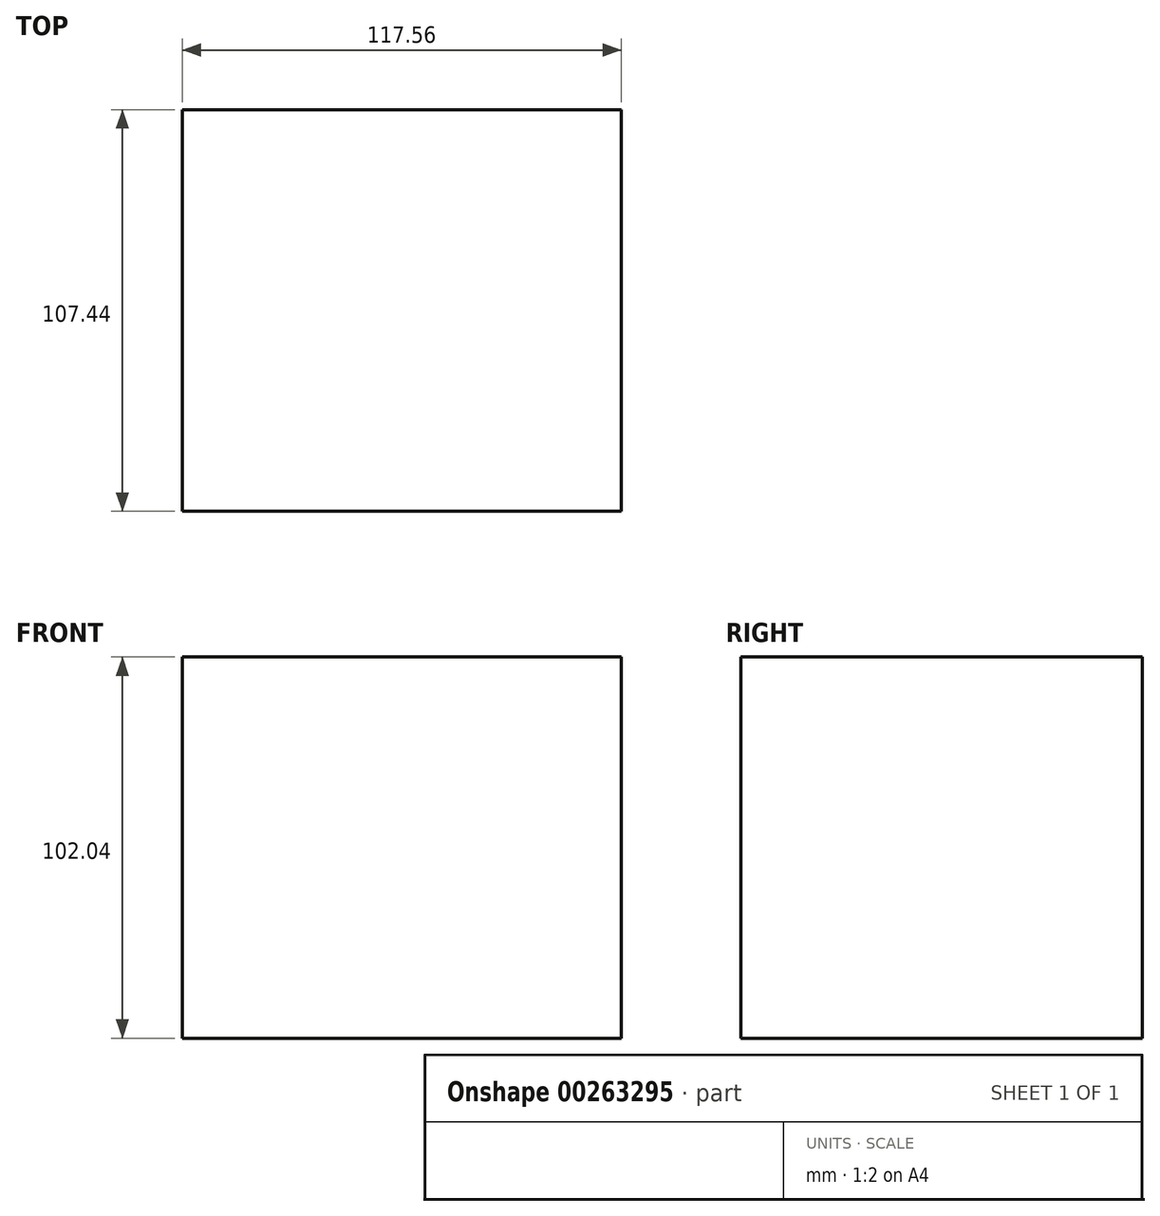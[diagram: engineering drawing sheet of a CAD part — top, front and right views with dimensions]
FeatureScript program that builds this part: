
annotation { "Feature Type Name" : "Feature", "Feature Type Description" : "" }
export const myFeature = defineFeature(function(context is Context, id is Id, definition is map)
    precondition{}
    {
        {
            var Q0;
            Q0=qCreatedBy(makeId("Front.planeOp"),FACE);
            var sketch = newSketch(context, id + "F0", { "sketchPlane" : qUnion([Q0])});
            skLineSegment(sketch, "E0.bottom", {"start": v(-60.76, 49.92) * mm, "end": v(56.8, 49.92) * mm});
            skLineSegment(sketch, "E0.top", {"start": v(-60.76, -52.12) * mm, "end": v(56.8, -52.12) * mm});
            skLineSegment(sketch, "E0.left", {"start": v(-60.76, 49.92) * mm, "end": v(-60.76, -52.12) * mm});
            skLineSegment(sketch, "E0.right", {"start": v(56.8, 49.92) * mm, "end": v(56.8, -52.12) * mm});
            skSolve(sketch);
        }
        {
            var Q0;
            Q0=makeQuery(id+"F0.imprint","IMPRINT",FACE,{"disambiguationData":[TD([[makeQuery(id+"F0.imprint","IMPRINT",EDGE,{"derivedFrom":sQuery(id+"F0.wireOp",EDGE,"E0.bottom")}),-1.0]])]});
            extrude(context, id + "F1", {"entities" : qUnion([Q0]), "depth" : 82.04 * mm, "hasSecondDirection" : true, "secondDirectionOppositeDirection" : true, "secondDirectionDepth" : 25.4 * mm});
        }
    });
